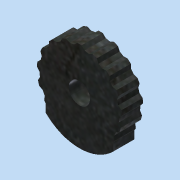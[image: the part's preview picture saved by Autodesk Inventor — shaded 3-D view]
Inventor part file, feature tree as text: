
AUTODESK INVENTOR PART (.ipt)
format: ipt  version: 2015 (Build 190159000, 159)  size: 178,176 bytes
history: native  units: in
note: dims shown in document units (in); Inventor stores cm internally (conversion verified against a paired STEP export)
features: extrude x3, sketch x2, other x1, pattern_circular x1
ambient origin geometry x8: Origin, YZ Plane, XZ Plane, XY Plane, X Axis, Y Axis, Z Axis, Center Point
bodies: Solid1 (feature_tree)
feature tree (7):
  other  "CaseRight.ipt"
  sketch  "Sketch2"  dims[d0=0.3937in d1=1.0in]
  extrude  "Extrusion1"  Depth=0.3937in
  extrude  "Extrusion2"  TaperAngle=15.0deg  [1 undecoded]
  pattern_circular  "Circular Pattern1"  [2 undecoded]
  extrude  "Extrusion3"  Depth=0.25in TaperAngle=0.0deg
  sketch  "Sketch3"  dims[d2=0.0312in d3=15.0deg d4=0.0412in d5=0.25in d6=0.0in d7=0.25in d8=0.0in d9=6.7492in d10=360.0deg d12=0.25in d13=90.0deg d14=1.125in d15=0.25in d16=0.0in]
note: 3 required parameter values undecoded (feature->parameter linkage not recoverable at this tier; creation-order binding heuristic only, values carry confidence <= 0.55)
